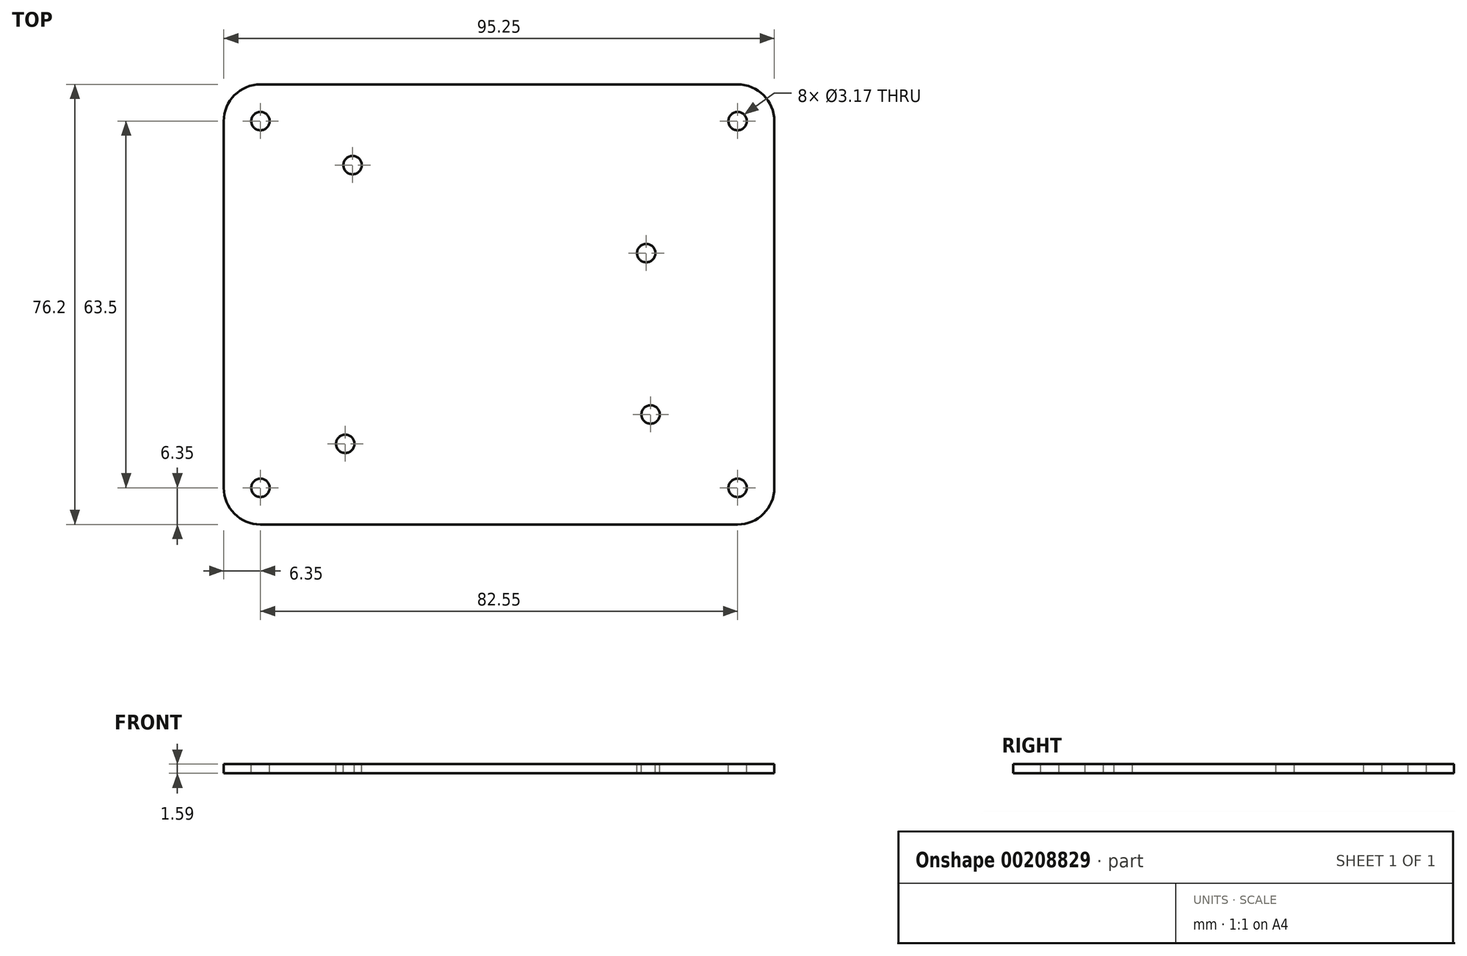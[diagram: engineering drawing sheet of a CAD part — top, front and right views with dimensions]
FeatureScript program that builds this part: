
annotation { "Feature Type Name" : "Feature", "Feature Type Description" : "" }
export const myFeature = defineFeature(function(context is Context, id is Id, definition is map)
    precondition{}
    {
        {
            var Q0;
            Q0=qCreatedBy(makeId("Top.planeOp"),FACE);
            var sketch = newSketch(context, id + "F0", { "sketchPlane" : qUnion([Q0])});
            skLineSegment(sketch, "E0.bottom", {"start": v(6.35, 0) * mm, "end": v(88.9, 0) * mm});
            skLineSegment(sketch, "E0.top", {"start": v(6.35, 76.2) * mm, "end": v(88.9, 76.2) * mm});
            skLineSegment(sketch, "E0.left", {"start": v(0, 6.35) * mm, "end": v(0, 69.85) * mm});
            skLineSegment(sketch, "E0.right", {"start": v(95.25, 6.35) * mm, "end": v(95.25, 69.85) * mm});
            skPoint(sketch, "E1.visualSharp", {"position": v(0, 76.2) * mm});
            skArc(sketch, "E1.filletArc", {"start": v(6.35, 76.2) * mm, "mid": v(1.86, 74.34) * mm, "end": v(0, 69.85) * mm});
            skPoint(sketch, "E2.visualSharp", {"position": v(95.25, 76.2) * mm});
            skArc(sketch, "E2.filletArc", {"start": v(95.25, 69.85) * mm, "mid": v(93.4, 74.34) * mm, "end": v(88.9, 76.2) * mm});
            skPoint(sketch, "E3.visualSharp", {"position": v(95.25, 0) * mm});
            skArc(sketch, "E3.filletArc", {"start": v(88.9, 0) * mm, "mid": v(93.4, 1.86) * mm, "end": v(95.25, 6.35) * mm});
            skPoint(sketch, "E4.visualSharp", {"position": v(0, 0) * mm});
            skArc(sketch, "E4.filletArc", {"start": v(0, 6.35) * mm, "mid": v(1.86, 1.86) * mm, "end": v(6.35, 0) * mm});
            skPoint(sketch, "E5", {"position": v(21.02, 13.97) * mm});
            skPoint(sketch, "E6", {"position": v(73.85, 19.05) * mm});
            skPoint(sketch, "E7", {"position": v(73.1, 47) * mm});
            skPoint(sketch, "E8", {"position": v(22.3, 62.23) * mm});
            skSolve(sketch);
        }
        {
            var Q0;
            Q0=makeQuery(id+"F0.imprint","IMPRINT",FACE,{"disambiguationData":[TD([[makeQuery(id+"F0.imprint","IMPRINT",EDGE,{"derivedFrom":sQuery(id+"F0.wireOp",EDGE,"E0.bottom")}),1.0]])]});
            extrude(context, id + "F1", {"entities" : qUnion([Q0]), "oppositeDirection" : true, "depth" : 1.59 * mm});
        }
        {
            var Q0;
            Q0=sQuery(id+"F0.wireOp",VERTEX,"E1.filletArc.center");
            var Q1;
            Q1=sQuery(id+"F0.wireOp",VERTEX,"E8");
            var Q2;
            Q2=sQuery(id+"F0.wireOp",VERTEX,"E7");
            var Q3;
            Q3=sQuery(id+"F0.wireOp",VERTEX,"E2.filletArc.center");
            var Q4;
            Q4=sQuery(id+"F0.wireOp",VERTEX,"E3.filletArc.center");
            var Q5;
            Q5=sQuery(id+"F0.wireOp",VERTEX,"E6");
            var Q6;
            Q6=sQuery(id+"F0.wireOp",VERTEX,"E5");
            var Q7;
            Q7=sQuery(id+"F0.wireOp",VERTEX,"E4.filletArc.center");
            var Q8;
            Q8=makeQuery(id+"F1.opExtrude","SWEPT_BODY",BODY,{"disambiguationData":[OSD([sQuery(id+"F0.wireOp",EDGE,"E0.bottom"),sQuery(id+"F0.wireOp",EDGE,"E0.top"),sQuery(id+"F0.wireOp",EDGE,"E0.left"),sQuery(id+"F0.wireOp",EDGE,"E0.right"),sQuery(id+"F0.wireOp",EDGE,"E1.filletArc"),sQuery(id+"F0.wireOp",EDGE,"E2.filletArc"),sQuery(id+"F0.wireOp",EDGE,"E3.filletArc"),sQuery(id+"F0.wireOp",EDGE,"E4.filletArc")])]});
            hole(context, id + "F2", {"style" : HoleStyle.SIMPLE, "endStyle" : HoleEndStyle.THROUGH, "holeDiameter" : 3.17 * mm, "locations" : qUnion([Q0, Q1, Q2, Q3, Q4, Q5, Q6, Q7]), "scope" : qUnion([Q8]), "isTappedThrough" : true});
        }
    });
